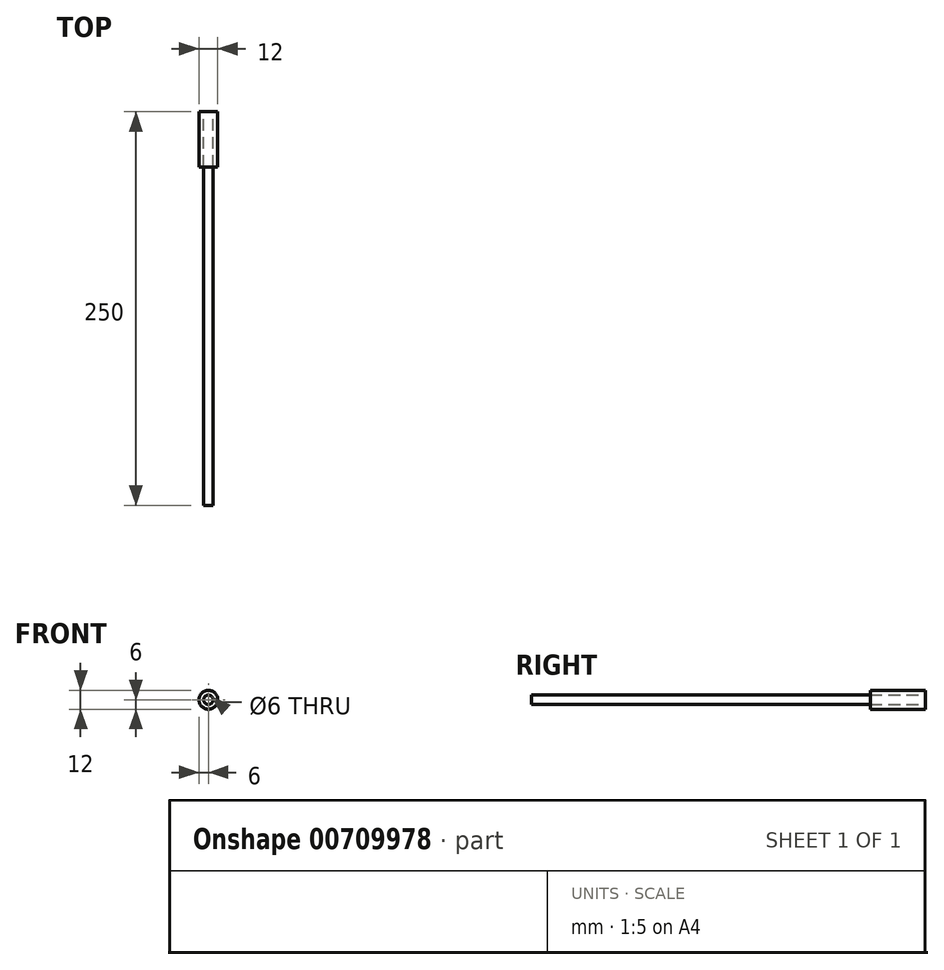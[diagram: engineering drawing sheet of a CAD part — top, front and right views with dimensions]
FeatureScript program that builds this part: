
annotation { "Feature Type Name" : "Feature", "Feature Type Description" : "" }
export const myFeature = defineFeature(function(context is Context, id is Id, definition is map)
    precondition{}
    {
        {
            var Q0;
            Q0=qCreatedBy(makeId("Front.planeOp"),FACE);
            var sketch = newSketch(context, id + "F0", { "sketchPlane" : qUnion([Q0])});
            skCircle(sketch, "E0", {"center": v(0, 0) * mm, "radius": 6 * mm});
            skCircle(sketch, "E1", {"center": v(0, 0) * mm, "radius": 3 * mm});
            skSolve(sketch);
        }
        {
            var Q0;
            Q0=makeQuery(id+"F0.imprint","IMPRINT",FACE,{"disambiguationData":[TD([[makeQuery(id+"F0.imprint","IMPRINT",EDGE,{"derivedFrom":sQuery(id+"F0.wireOp",EDGE,"E0")}),1.0]])]});
            extrude(context, id + "F1", {"entities" : qUnion([Q0]), "depth" : 35 * mm, "offsetDistance" : 25 * mm});
        }
        {
            var Q0;
            Q0=makeQuery(id+"F0.imprint","IMPRINT",FACE,{"disambiguationData":[TD([[makeQuery(id+"F0.imprint","IMPRINT",EDGE,{"derivedFrom":sQuery(id+"F0.wireOp",EDGE,"E1")}),1.0]])]});
            extrude(context, id + "F2", {"entities" : qUnion([Q0]), "depth" : 250 * mm, "offsetDistance" : 25 * mm});
        }
    });
